# Revit family: IS_Connect_N1385_BIM_DE
name_source: partatom
category: Plumbing Fixtures
revit_build: Autodesk Revit MEP 2016 (Build: 20161004_0715(x64)
units: mm (PartAtom-declared; Revit-internal decimal feet)

## family parameters
Always vertical = No
Cut with Voids When Loaded = No
Part Type = Normal
Room Calculation Point = No
Round Connector Dimension = Use Diameter
Shared = No
Work Plane-Based = No

## types (1)
- N1385AA CONNECT towel rail, 300mm
    BIMobject category = Accessories
    BOSUseNativeGeometries = 1
    Brand url = http://www.idealstandard.co.uk
    EAN code = https://8014140353706
    Edition number = 1
    IFC Classification = Sanitary Terminal
    Installation instructions = http://www.idealstandard.de
    Manufacturer name = Ideal Standard
    Model = N1385AA
    NBS Reference Code = 35-75-90
    NBS Reference Description = Towel Rails
    Nominal height = 18
    Nominal width = 300
    NominalDepth = 0 mm  [stored 0 ft]
    NominalHeight = 18 mm  [stored 0.0590551 ft]
    NominalLength = 85 mm  [stored 0.278871 ft]
    NominalWidth = 300 mm  [stored 0.984252 ft]
    OmniClass Code = 23-31 25 00
    OmniClass Description = Toilet and Bath Specialties
    Product Guid = f37da236-8e34-464d-b7bc-cbc9abd8b293
    Product SKU = N1385
    Product data url = https://bimobject.com
    Product family = CONNECT
    Product group = Accessories
    Product name = CONNECT towel rail, 300mm
    Product url = http://www.idealstandard.de
    QR code = http://bimobject.com
    Size = 300x85x18 mm
    Technical description = http://www.idealstandard.de
    Uniclass 1.4 Code = L8245
    Uniclass 1.4 Description = Towel rails
    Uniclass 2.0 Code = PR-35-75-90
    Uniclass 2.0 Description = Towel Rails
    Uniclass 2015 Code = Pr_40_20_76_90
    Uniclass 2015 Name = Towel rails
    Weight Net (Kg) = 0.22

note: [stored X ft] marks values corroborated as IEEE doubles in the binary element streams (Revit-internal decimal feet)

## geometry (parser evidence)
native form markers: Blend x4, Sweep x1
no freeform markers — native parametric forms only
